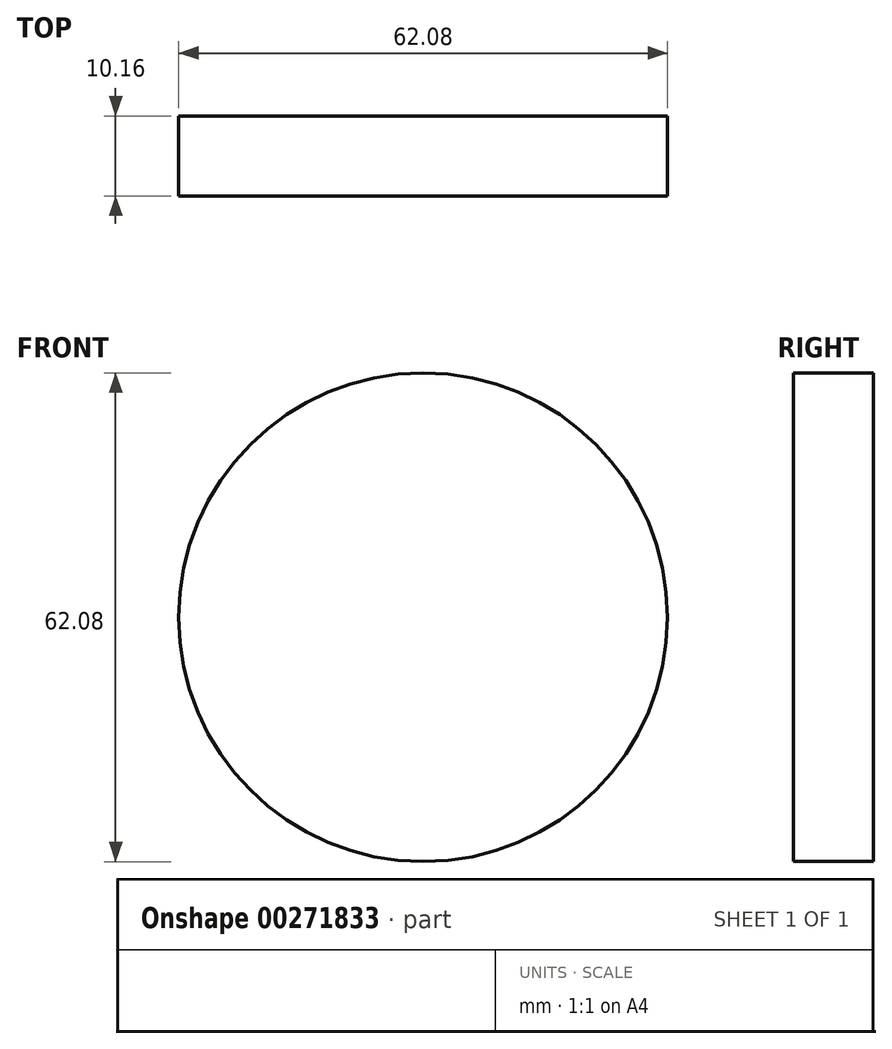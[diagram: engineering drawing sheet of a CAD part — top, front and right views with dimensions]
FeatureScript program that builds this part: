
annotation { "Feature Type Name" : "Feature", "Feature Type Description" : "" }
export const myFeature = defineFeature(function(context is Context, id is Id, definition is map)
    precondition{}
    {
        {
            var Q0;
            Q0=qCreatedBy(makeId("Top.planeOp"),FACE);
            var sketch = newSketch(context, id + "F0", { "sketchPlane" : qUnion([Q0])});
            skCircle(sketch, "E0", {"center": v(0, 0) * mm, "radius": 15.77 * mm});
            skSolve(sketch);
        }
        {
            var Q0;
            Q0=sQuery(id+"F0.wireOp",EDGE,"E0");
            extrude(context, id + "F1", {"bodyType" : ToolBodyType.SURFACE, "surfaceEntities" : qUnion([Q0]), "depth" : 25.4 * mm, "hasSecondDirection" : true, "secondDirectionOppositeDirection" : true, "secondDirectionDepth" : 25.4 * mm});
        }
        {
            var Q0;
            Q0=qCreatedBy(makeId("Front.planeOp"),FACE);
            var sketch = newSketch(context, id + "F2", { "sketchPlane" : qUnion([Q0])});
            skCircle(sketch, "E1", {"center": v(0, 0) * mm, "radius": 31.04 * mm});
            skSolve(sketch);
        }
        {
            var Q0;
            Q0 = qSketchRegion(id + "F2", true);
            extrude(context, id + "F3", {"entities" : qUnion([Q0]), "depth" : 5.08 * mm, "hasSecondDirection" : true, "secondDirectionOppositeDirection" : true, "secondDirectionDepth" : 5.08 * mm});
        }
        {
            var Q0;
            Q0=makeQuery(id+"F3.opExtrude","CAP_FACE",FACE,{"disambiguationData":[OSD([sQuery(id+"F2.wireOp",EDGE,"E1")])],"isStart":false});
            cPlane(context, id + "F4", {"entities" : qUnion([Q0]), "cplaneType" : CPlaneType.OFFSET, "offset" : 0 * mm, "width" : 152.4 * mm, "height" : 152.4 * mm});
        }
    });
